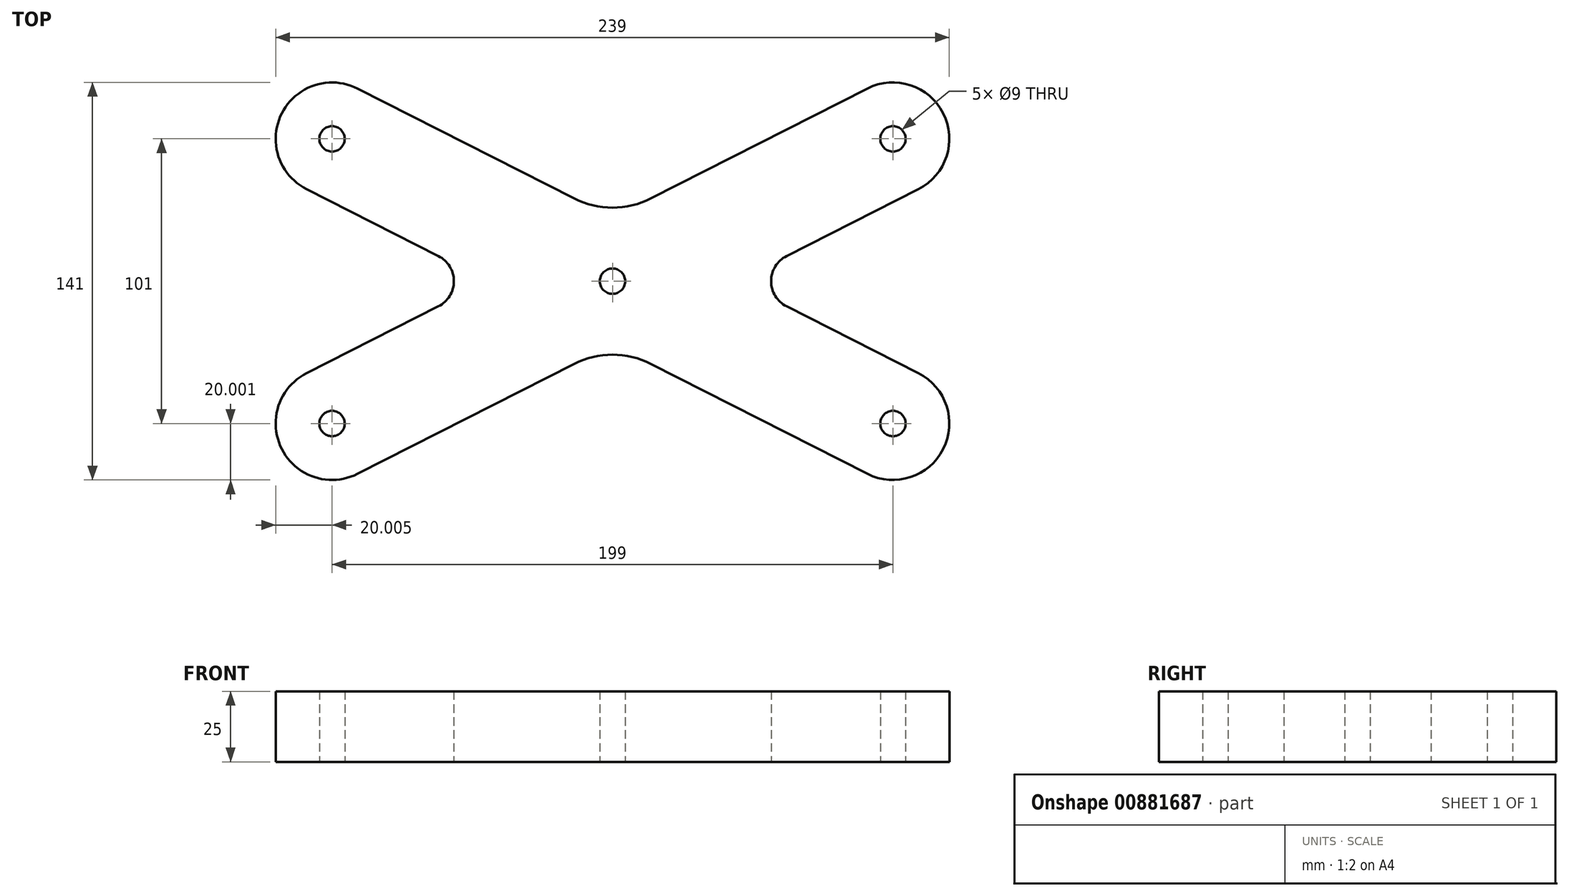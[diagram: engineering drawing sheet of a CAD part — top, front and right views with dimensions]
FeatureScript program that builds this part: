
annotation { "Feature Type Name" : "Feature", "Feature Type Description" : "" }
export const myFeature = defineFeature(function(context is Context, id is Id, definition is map)
    precondition{}
    {
        {
            var Q0;
            Q0=qCreatedBy(makeId("Top.planeOp"),FACE);
            var sketch = newSketch(context, id + "F0", { "sketchPlane" : qUnion([Q0])});
            skLineSegment(sketch, "E0.bottom", {"start": v(-150.6, 59.7) * mm, "end": v(48.4, 59.7) * mm, "construction": true});
            skLineSegment(sketch, "E0.right", {"start": v(48.4, 59.7) * mm, "end": v(48.4, 55.2) * mm});
            skCircle(sketch, "E1", {"center": v(-150.6, -41.3) * mm, "radius": 4.5 * mm});
            skCircle(sketch, "E2.0.1.0", {"center": v(-150.6, 59.7) * mm, "radius": 4.5 * mm});
            skCircle(sketch, "E2.1.0.0", {"center": v(48.4, -41.3) * mm, "radius": 4.5 * mm});
            skCircle(sketch, "E2.1.1.0", {"center": v(48.4, 59.7) * mm, "radius": 4.5 * mm});
            skArc(sketch, "E3", {"start": v(-159.65, -23.46) * mm, "mid": v(-168.43, -50.35) * mm, "end": v(-141.54, -59.13) * mm});
            skArc(sketch, "E4.0.1.0", {"start": v(-141.54, 77.54) * mm, "mid": v(-168.43, 68.75) * mm, "end": v(-159.65, 41.87) * mm});
            skArc(sketch, "E4.1.0.0", {"start": v(39.35, -59.13) * mm, "mid": v(66.24, -50.35) * mm, "end": v(57.46, -23.46) * mm});
            skArc(sketch, "E4.1.1.0", {"start": v(57.46, 41.87) * mm, "mid": v(66.24, 68.75) * mm, "end": v(39.35, 77.54) * mm});
            skLineSegment(sketch, "E5", {"start": v(-141.54, 77.54) * mm, "end": v(-64.67, 38.52) * mm});
            skLineSegment(sketch, "E6", {"start": v(-159.65, 41.87) * mm, "end": v(-112.86, 18.12) * mm});
            skLineSegment(sketch, "E7", {"start": v(-159.65, -23.46) * mm, "end": v(-112.86, 0.28) * mm});
            skLineSegment(sketch, "E8", {"start": v(-141.54, -59.13) * mm, "end": v(-64.67, -20.12) * mm});
            skLineSegment(sketch, "E9.trimOffspring", {"start": v(-37.52, -20.12) * mm, "end": v(39.35, -59.13) * mm});
            skLineSegment(sketch, "E10.trimOffspring", {"start": v(10.67, 0.28) * mm, "end": v(57.46, -23.46) * mm});
            skLineSegment(sketch, "E11.trimOffspring", {"start": v(-37.52, 38.52) * mm, "end": v(39.35, 77.54) * mm});
            skLineSegment(sketch, "E12.trimOffspring", {"start": v(10.67, 18.12) * mm, "end": v(57.46, 41.87) * mm});
            skPoint(sketch, "E13.visualSharp", {"position": v(-51.1, 31.63) * mm});
            skArc(sketch, "E13.filletArc", {"start": v(-64.67, 38.52) * mm, "mid": v(-51.1, 35.27) * mm, "end": v(-37.52, 38.52) * mm});
            skPoint(sketch, "E14.visualSharp", {"position": v(-51.1, -13.23) * mm});
            skArc(sketch, "E14.filletArc", {"start": v(-37.52, -20.12) * mm, "mid": v(-51.1, -16.87) * mm, "end": v(-64.67, -20.12) * mm});
            skPoint(sketch, "E15.visualSharp", {"position": v(-6.9, 9.2) * mm});
            skArc(sketch, "E15.filletArc", {"start": v(10.67, 18.12) * mm, "mid": v(5.2, 9.2) * mm, "end": v(10.67, 0.28) * mm});
            skPoint(sketch, "E16.visualSharp", {"position": v(-95.29, 9.2) * mm});
            skArc(sketch, "E16.filletArc", {"start": v(-112.86, 0.28) * mm, "mid": v(-107.38, 9.2) * mm, "end": v(-112.86, 18.12) * mm});
            skLineSegment(sketch, "E17.trimOffspring", {"start": v(48.4, 37.27) * mm, "end": v(48.4, -41.3) * mm, "construction": true});
            skCircle(sketch, "E18", {"center": v(-51.1, 9.2) * mm, "radius": 4.5 * mm});
            skSolve(sketch);
        }
        {
            var Q0;
            Q0 = qSketchRegion(id + "F0", true);
            extrude(context, id + "F1", {"entities" : qUnion([Q0]), "depth" : 25 * mm, "offsetDistance" : 25 * mm});
        }
    });
